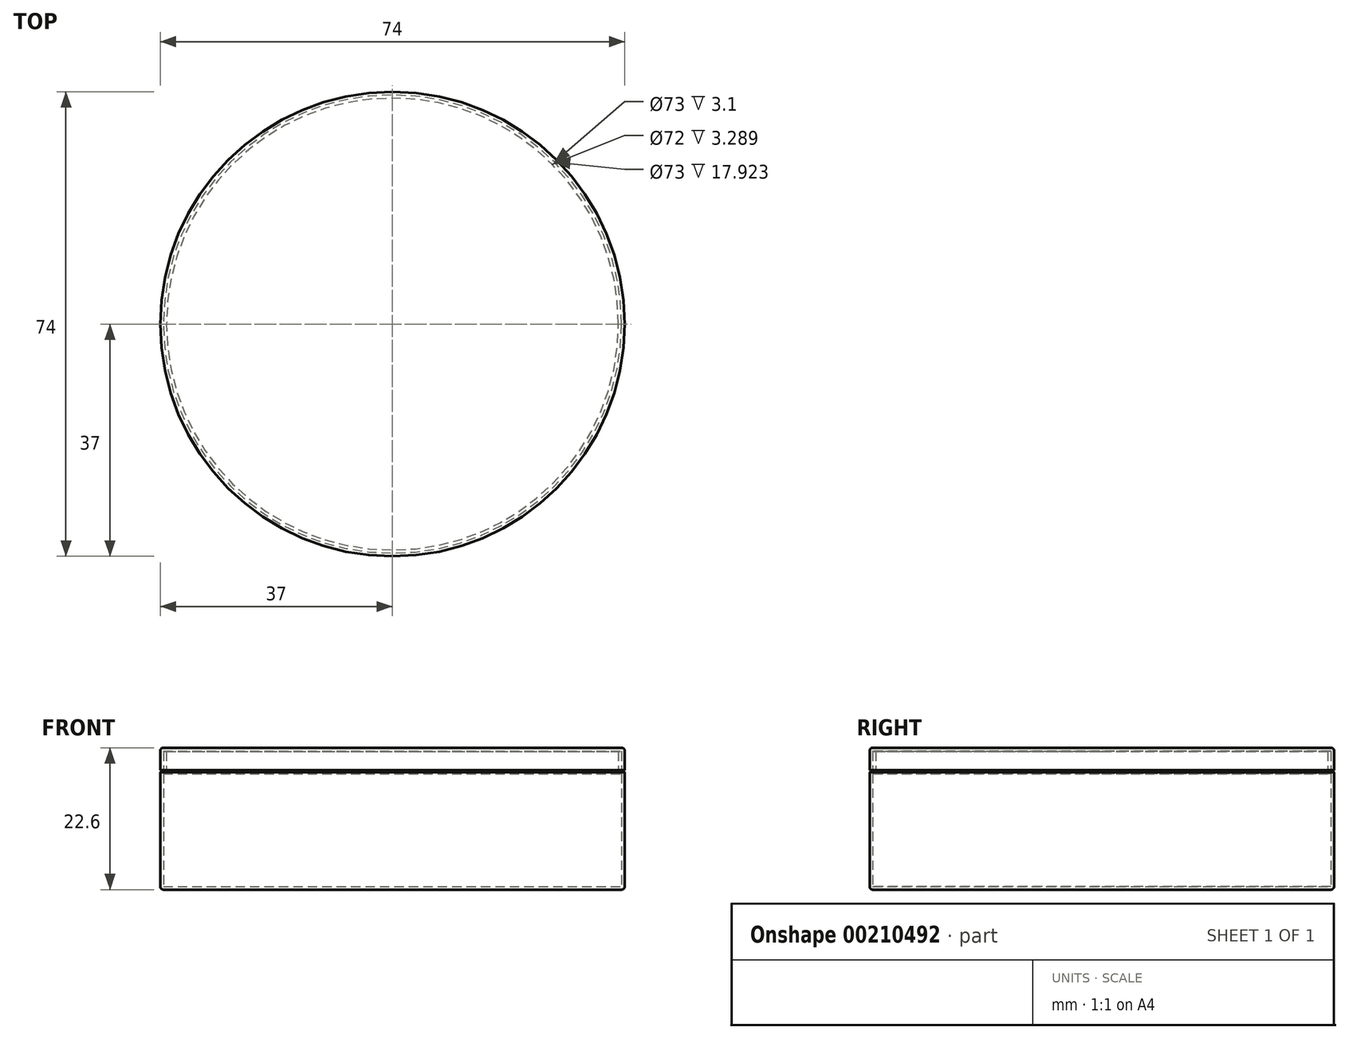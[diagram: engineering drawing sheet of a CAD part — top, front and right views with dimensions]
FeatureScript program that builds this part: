
annotation { "Feature Type Name" : "Feature", "Feature Type Description" : "" }
export const myFeature = defineFeature(function(context is Context, id is Id, definition is map)
    precondition{}
    {
        {
            var Q0;
            Q0=qCreatedBy(makeId("Front.planeOp"),FACE);
            var sketch = newSketch(context, id + "F0", { "sketchPlane" : qUnion([Q0])});
            skLineSegment(sketch, "E0", {"start": v(0, 0) * mm, "end": v(37, 0) * mm});
            skLineSegment(sketch, "E1", {"start": v(37, 0) * mm, "end": v(37, 18.71) * mm});
            skLineSegment(sketch, "E2", {"start": v(37, 18.71) * mm, "end": v(36.5, 19) * mm});
            skLineSegment(sketch, "E3", {"start": v(36.5, 19) * mm, "end": v(36.5, 22) * mm});
            skLineSegment(sketch, "E4.0", {"start": v(36, 18.71) * mm, "end": v(36, 22) * mm});
            skLineSegment(sketch, "E4.1", {"start": v(36.5, 18.42) * mm, "end": v(36, 18.71) * mm});
            skLineSegment(sketch, "E4.2", {"start": v(36.5, 0.5) * mm, "end": v(36.5, 18.42) * mm});
            skLineSegment(sketch, "E4.3", {"start": v(0, 0.5) * mm, "end": v(36.5, 0.5) * mm});
            skLineSegment(sketch, "E5", {"start": v(36, 22) * mm, "end": v(36.5, 22) * mm});
            skLineSegment(sketch, "E6", {"start": v(0, 0) * mm, "end": v(0, 0.5) * mm});
            skLineSegment(sketch, "E7", {"start": v(0, 0) * mm, "end": v(0, 22) * mm, "construction": true});
            skSolve(sketch);
        }
        {
            var Q0;
            Q0=makeQuery(id+"F0.imprint","IMPRINT",FACE,{"disambiguationData":[TD([[makeQuery(id+"F0.imprint","IMPRINT",EDGE,{"derivedFrom":sQuery(id+"F0.wireOp",EDGE,"E0")}),1.0]])]});
            var Q1;
            Q1=sQuery(id+"F0.wireOp",EDGE,"E7");
            revolve(context, id + "F1", {"entities" : qUnion([Q0]), "axis" : qUnion([Q1]), "revolveType" : RevolveType.FULL});
        }
        {
            var Q0;
            Q0=makeQuery(id+"F1.opRevolve","SWEPT_EDGE",EDGE,{"disambiguationData":[OSD([sQuery(id+"F0.wireOp",EDGE,"E0"),sQuery(id+"F0.wireOp",EDGE,"E1")])]});
            fillet(context, id + "F2", {"entities" : qUnion([Q0]), "radius" : 0.5 * mm, "tangentPropagation" : true, "allowEdgeOverflow" : false});
        }
        {
            var Q0;
            Q0=qCreatedBy(makeId("Front.planeOp"),FACE);
            var sketch = newSketch(context, id + "F3", { "sketchPlane" : qUnion([Q0])});
            skLineSegment(sketch, "E8", {"start": v(36.5, 22.1) * mm, "end": v(36.5, 19) * mm});
            skLineSegment(sketch, "E9", {"start": v(36.5, 22.1) * mm, "end": v(0, 22.1) * mm});
            skLineSegment(sketch, "E10.0", {"start": v(37, 22.6) * mm, "end": v(37, 19) * mm});
            skLineSegment(sketch, "E10.1", {"start": v(37, 22.6) * mm, "end": v(0, 22.6) * mm});
            skLineSegment(sketch, "E11", {"start": v(37, 19) * mm, "end": v(36.5, 19) * mm});
            skLineSegment(sketch, "E12", {"start": v(0, 22.1) * mm, "end": v(0, 22.6) * mm});
            skLineSegment(sketch, "E13", {"start": v(0, 0) * mm, "end": v(0, 22.6) * mm, "construction": true});
            skSolve(sketch);
        }
        {
            var Q0;
            Q0=qSketchRegion(id+"F3",true);
            var Q1;
            Q1=sQuery(id+"F3.wireOp",EDGE,"E13");
            revolve(context, id + "F4", {"entities" : qUnion([Q0]), "axis" : qUnion([Q1]), "revolveType" : RevolveType.FULL});
        }
        {
            var Q0;
            Q0=makeQuery(id+"F4.opRevolve","SWEPT_EDGE",EDGE,{"disambiguationData":[OSD([sQuery(id+"F3.wireOp",EDGE,"E10.0"),sQuery(id+"F3.wireOp",EDGE,"E10.1")])]});
            fillet(context, id + "F5", {"entities" : qUnion([Q0]), "radius" : 0.5 * mm, "tangentPropagation" : true, "allowEdgeOverflow" : false});
        }
    });
